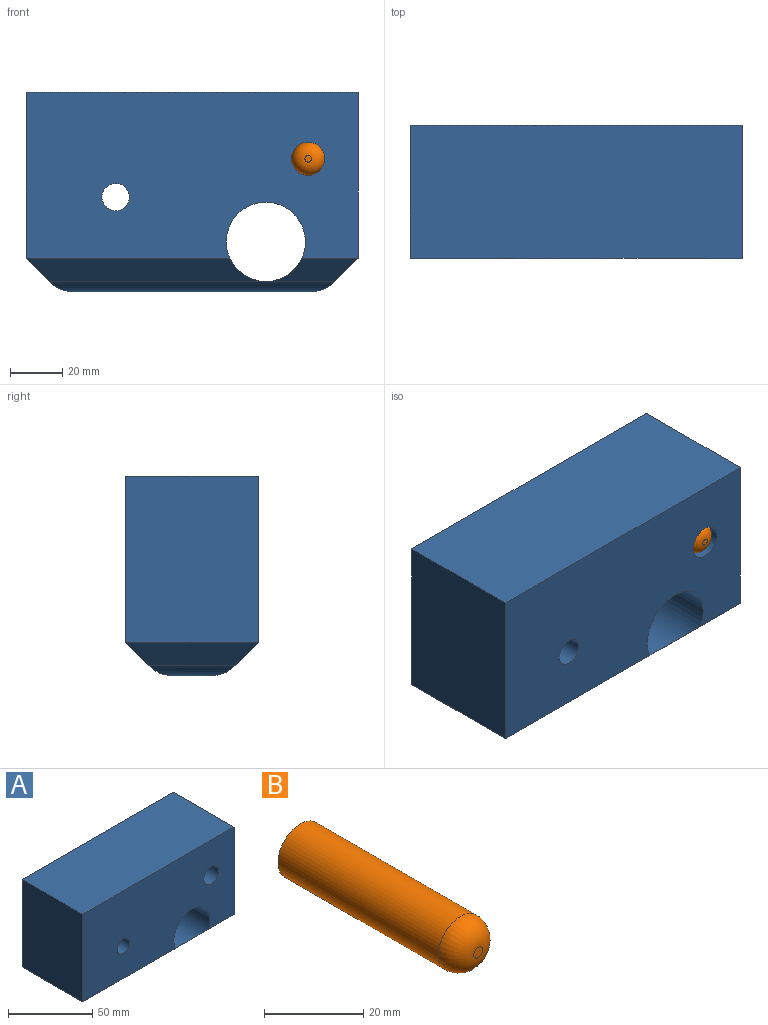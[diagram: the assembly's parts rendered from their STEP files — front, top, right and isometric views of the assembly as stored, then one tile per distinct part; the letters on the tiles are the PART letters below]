
ASSEMBLY  parts=2 mates=1
PART A: 17 faces, bbox 127x50.8x76.2 mm
  f0: plane 63.5x50.8mm, normal (-1,0,0), area 3225.8mm2, adj f5,f6,f7,f10
  f1: plane 91.08x14.88mm, normal (0,0,-1), area 1355.2mm2, adj f13,f14,f15,f16
  f2: plane 63.5x50.8mm, normal (1,0,0), area 3225.8mm2, adj f5,f6,f7,f11
  f3: cylinder r=6.35mm len=50.8mm, axis (0,1,0), area 2026.8mm2, adj f6,f7
  f4: cylinder r=5.22mm len=50.8mm, axis (0,1,0), area 1667.6mm2, adj f6,f7
  f5: plane 127x50.8mm, normal (0,0,1), area 6451.6mm2, adj f0,f2,f6,f7
  f6: plane 127x63.5mm, normal (0,-1,0), area 7306.6mm2, adj f0,f2,f3,f4,f5,f8,f9
  f7: plane 127x63.5mm, normal (0,1,0), area 7306.6mm2, adj f0,f2,f3,f4,f5,f8,f12
  f8: cylinder r=15.14mm len=50.8mm, axis (0,-1,0), area 4435.1mm2, adj f6,f7,f9,f12
  f9: plane 127x8.98mm, normal (0,-0.71,-0.71), area 1252mm2, adj f6,f8,f10,f11,f14
  f10: plane 50.8x8.98mm, normal (-0.71,0,-0.71), area 531.1mm2, adj f0,f9,f12,f16
  f11: plane 50.8x8.98mm, normal (0.71,0,-0.71), area 531.1mm2, adj f2,f9,f12,f13
  f12: plane 127x8.98mm, normal (0,0.71,-0.71), area 1252mm2, adj f7,f8,f10,f11,f15
  f13: cylinder r=12.7mm len=32.84mm, axis (0,1,0), area 242.9mm2, adj f1,f11,f14,f15
  f14: cylinder r=12.7mm len=109.04mm, axis (1,0,0), area 1003mm2, adj f1,f9,f13,f16
  f15: cylinder r=12.7mm len=109.04mm, axis (1,0,0), area 1003mm2, adj f1,f12,f13,f16
  f16: cylinder r=12.7mm len=32.84mm, axis (0,1,0), area 242.9mm2, adj f1,f10,f14,f15
PART B: 4 faces, bbox 12.7x50.8x12.7 mm
  f0: cylinder r=6.35mm len=45.72mm, axis (0,1,0), area 1824.1mm2, adj f2,f3
  f1: plane 2.54x2.54mm, normal (0,-1,0), area 5.1mm2, adj f3
  f2: plane 12.7x12.7mm, normal (0,1,0), area 126.7mm2, adj f0
  f3: torus R=1.27mm, axis (0,-1,0), area 225.8mm2, adj f0,f1
PLACE A t=(-21.23,-19.87,18.73)mm fixed
PLACE B t=(21.57,-19.87,-35.39)mm
MATE fastened B.f0 <-> A.f3  axis (0,1,0) through (21.57,-19.87,-35.39)mm
